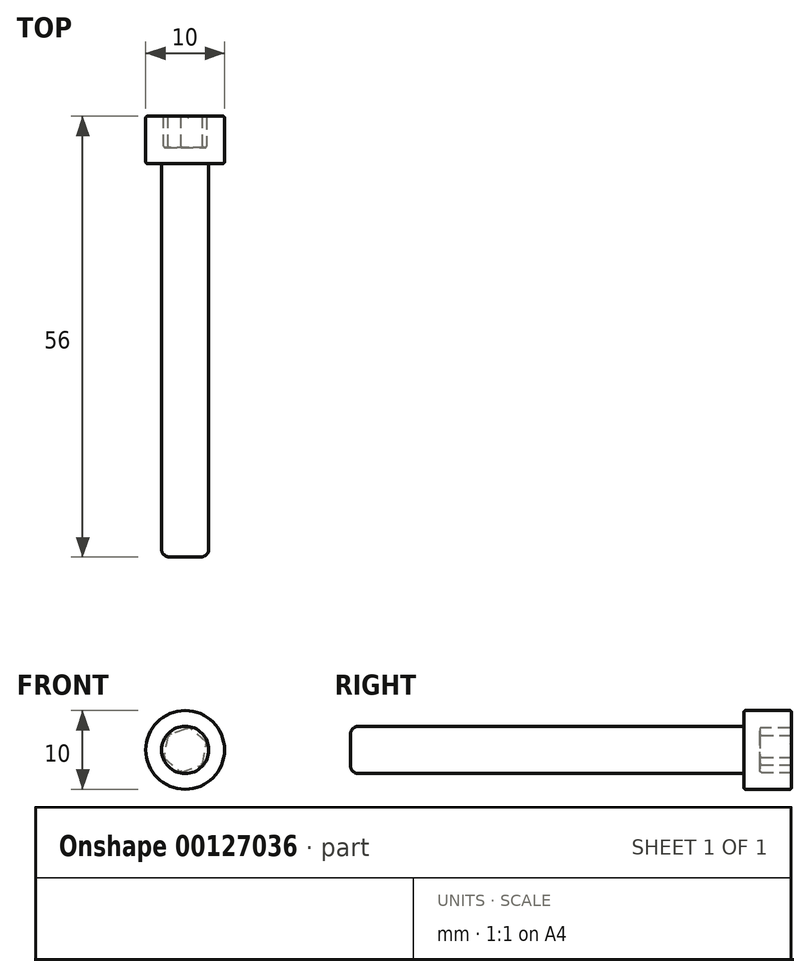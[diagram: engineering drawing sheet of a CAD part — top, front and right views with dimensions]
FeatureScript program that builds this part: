
annotation { "Feature Type Name" : "Feature", "Feature Type Description" : "" }
export const myFeature = defineFeature(function(context is Context, id is Id, definition is map)
    precondition{}
    {
        {
            var Q0;
            Q0=qCreatedBy(makeId("Front.planeOp"),FACE);
            var sketch = newSketch(context, id + "F0", { "sketchPlane" : qUnion([Q0])});
            skCircle(sketch, "E0", {"center": v(0, 0) * mm, "radius": 3 * mm});
            skCircle(sketch, "E1", {"center": v(0, 0) * mm, "radius": 5 * mm});
            skSolve(sketch);
        }
        {
            var Q0;
            Q0=makeQuery(id+"F0.imprint","IMPRINT",FACE,{"disambiguationData":[TD([[makeQuery(id+"F0.imprint","IMPRINT",EDGE,{"derivedFrom":sQuery(id+"F0.wireOp",EDGE,"E0")}),1.0]])]});
            extrude(context, id + "F1", {"entities" : qUnion([Q0]), "depth" : 50 * mm});
        }
        {
            var Q0;
            Q0=makeQuery(id+"F0.imprint","IMPRINT",FACE,{"disambiguationData":[TD([[makeQuery(id+"F0.imprint","IMPRINT",EDGE,{"derivedFrom":sQuery(id+"F0.wireOp",EDGE,"E0")}),-1.0]])]});
            var Q1;
            Q1=makeQuery(id+"F0.imprint","IMPRINT",FACE,{"disambiguationData":[TD([[makeQuery(id+"F0.imprint","IMPRINT",EDGE,{"derivedFrom":sQuery(id+"F0.wireOp",EDGE,"E0")}),1.0]])]});
            extrude(context, id + "F2", {"entities" : qUnion([Q0, Q1]), "operationType" : NewBodyOperationType.ADD, "oppositeDirection" : true, "depth" : 6 * mm});
        }
        {
            var Q0;
            Q0=makeQuery(id+"F2.opExtrude","CAP_FACE",FACE,{"disambiguationData":[OSD([sQuery(id+"F0.wireOp",EDGE,"E1")])],"isStart":false});
            var sketch = newSketch(context, id + "F3", { "sketchPlane" : qUnion([Q0])});
            skPoint(sketch, "E2.0", {"position": v(0, 0) * mm});
            skCircle(sketch, "E3.cCircle", {"center": v(0, 0) * mm, "radius": 2.5 * mm, "construction": true});
            skLineSegment(sketch, "E3.0", {"start": v(-0.52, 2.84) * mm, "end": v(2.2, 1.87) * mm});
            skLineSegment(sketch, "E3.1", {"start": v(2.2, 1.87) * mm, "end": v(2.72, -0.97) * mm});
            skLineSegment(sketch, "E3.2", {"start": v(2.72, -0.97) * mm, "end": v(0.52, -2.84) * mm});
            skLineSegment(sketch, "E3.3", {"start": v(0.52, -2.84) * mm, "end": v(-2.2, -1.87) * mm});
            skLineSegment(sketch, "E3.4", {"start": v(-2.2, -1.87) * mm, "end": v(-2.72, 0.97) * mm});
            skLineSegment(sketch, "E3.5", {"start": v(-2.72, 0.97) * mm, "end": v(-0.52, 2.84) * mm});
            skPoint(sketch, "E3.0.midPoint", {"position": v(0.84, 2.36) * mm});
            skSolve(sketch);
        }
        {
            var Q0;
            Q0=makeQuery(id+"F3.imprint","IMPRINT",FACE,{"disambiguationData":[TD([[makeQuery(id+"F3.imprint","IMPRINT",EDGE,{"derivedFrom":sQuery(id+"F3.wireOp",EDGE,"E3.0")}),-1.0]])]});
            extrude(context, id + "F4", {"entities" : qUnion([Q0]), "operationType" : NewBodyOperationType.REMOVE, "oppositeDirection" : true, "depth" : 4 * mm});
        }
        {
            var Q0;
            Q0=makeQuery(id+"F2.opExtrude","CAP_EDGE",EDGE,{"disambiguationData":[OSD([sQuery(id+"F0.wireOp",EDGE,"E1")])],"isStart":false});
            var Q1;
            Q1=makeQuery(id+"F2.opExtrude","CAP_EDGE",EDGE,{"disambiguationData":[OSD([sQuery(id+"F0.wireOp",EDGE,"E1")])],"isStart":true});
            var Q2;
            Q2=makeQuery(id+"F4.boolean.opBoolean","COPY",EDGE,{"derivedFrom":makeQuery(id+"F4.opExtrude","CAP_EDGE",EDGE,{"disambiguationData":[OSD([sQuery(id+"F3.wireOp",EDGE,"E3.3")])],"isStart":true})});
            var Q3;
            Q3=makeQuery(id+"F4.boolean.opBoolean","COPY",EDGE,{"derivedFrom":makeQuery(id+"F4.opExtrude","CAP_EDGE",EDGE,{"disambiguationData":[OSD([sQuery(id+"F3.wireOp",EDGE,"E3.2")])],"isStart":true})});
            var Q4;
            Q4=makeQuery(id+"F4.boolean.opBoolean","COPY",EDGE,{"derivedFrom":makeQuery(id+"F4.opExtrude","CAP_EDGE",EDGE,{"disambiguationData":[OSD([sQuery(id+"F3.wireOp",EDGE,"E3.1")])],"isStart":true})});
            var Q5;
            Q5=makeQuery(id+"F4.boolean.opBoolean","COPY",EDGE,{"derivedFrom":makeQuery(id+"F4.opExtrude","CAP_EDGE",EDGE,{"disambiguationData":[OSD([sQuery(id+"F3.wireOp",EDGE,"E3.4")])],"isStart":true})});
            var Q6;
            Q6=makeQuery(id+"F4.boolean.opBoolean","COPY",EDGE,{"derivedFrom":makeQuery(id+"F4.opExtrude","CAP_EDGE",EDGE,{"disambiguationData":[OSD([sQuery(id+"F3.wireOp",EDGE,"E3.5")])],"isStart":true})});
            var Q7;
            Q7=makeQuery(id+"F4.boolean.opBoolean","COPY",EDGE,{"derivedFrom":makeQuery(id+"F4.opExtrude","CAP_EDGE",EDGE,{"disambiguationData":[OSD([sQuery(id+"F3.wireOp",EDGE,"E3.0")])],"isStart":true})});
            var Q8;
            Q8=makeQuery(id+"F4.boolean.opBoolean","COPY",EDGE,{"derivedFrom":makeQuery(id+"F4.opExtrude","CAP_EDGE",EDGE,{"disambiguationData":[OSD([sQuery(id+"F3.wireOp",EDGE,"E3.2")])],"isStart":false})});
            var Q9;
            Q9=makeQuery(id+"F4.boolean.opBoolean","COPY",EDGE,{"derivedFrom":makeQuery(id+"F4.opExtrude","CAP_EDGE",EDGE,{"disambiguationData":[OSD([sQuery(id+"F3.wireOp",EDGE,"E3.3")])],"isStart":false})});
            var Q10;
            Q10=makeQuery(id+"F4.boolean.opBoolean","COPY",EDGE,{"derivedFrom":makeQuery(id+"F4.opExtrude","CAP_EDGE",EDGE,{"disambiguationData":[OSD([sQuery(id+"F3.wireOp",EDGE,"E3.4")])],"isStart":false})});
            var Q11;
            Q11=makeQuery(id+"F4.boolean.opBoolean","COPY",FACE,{"derivedFrom":makeQuery(id+"F4.opExtrude","SWEPT_FACE",FACE,{"disambiguationData":[OSD([sQuery(id+"F3.wireOp",EDGE,"E3.5")])]})});
            var Q12;
            Q12=makeQuery(id+"F4.boolean.opBoolean","COPY",EDGE,{"derivedFrom":makeQuery(id+"F4.opExtrude","CAP_EDGE",EDGE,{"disambiguationData":[OSD([sQuery(id+"F3.wireOp",EDGE,"E3.0")])],"isStart":false})});
            var Q13;
            Q13=makeQuery(id+"F4.boolean.opBoolean","COPY",EDGE,{"derivedFrom":makeQuery(id+"F4.opExtrude","CAP_EDGE",EDGE,{"disambiguationData":[OSD([sQuery(id+"F3.wireOp",EDGE,"E3.1")])],"isStart":false})});
            fillet(context, id + "F5", {"entities" : qUnion([Q0, Q1, Q2, Q3, Q4, Q5, Q6, Q7, Q8, Q9, Q10, Q11, Q12, Q13]), "radius" : .2 * mm, "tangentPropagation" : true, "allowEdgeOverflow" : false});
        }
        {
            var Q0;
            Q0=makeQuery(id+"F1.opExtrude","CAP_EDGE",EDGE,{"disambiguationData":[OSD([sQuery(id+"F0.wireOp",EDGE,"E0")])],"isStart":false});
            fillet(context, id + "F6", {"entities" : qUnion([Q0]), "radius" : 1 * mm, "tangentPropagation" : true, "allowEdgeOverflow" : false});
        }
    });
